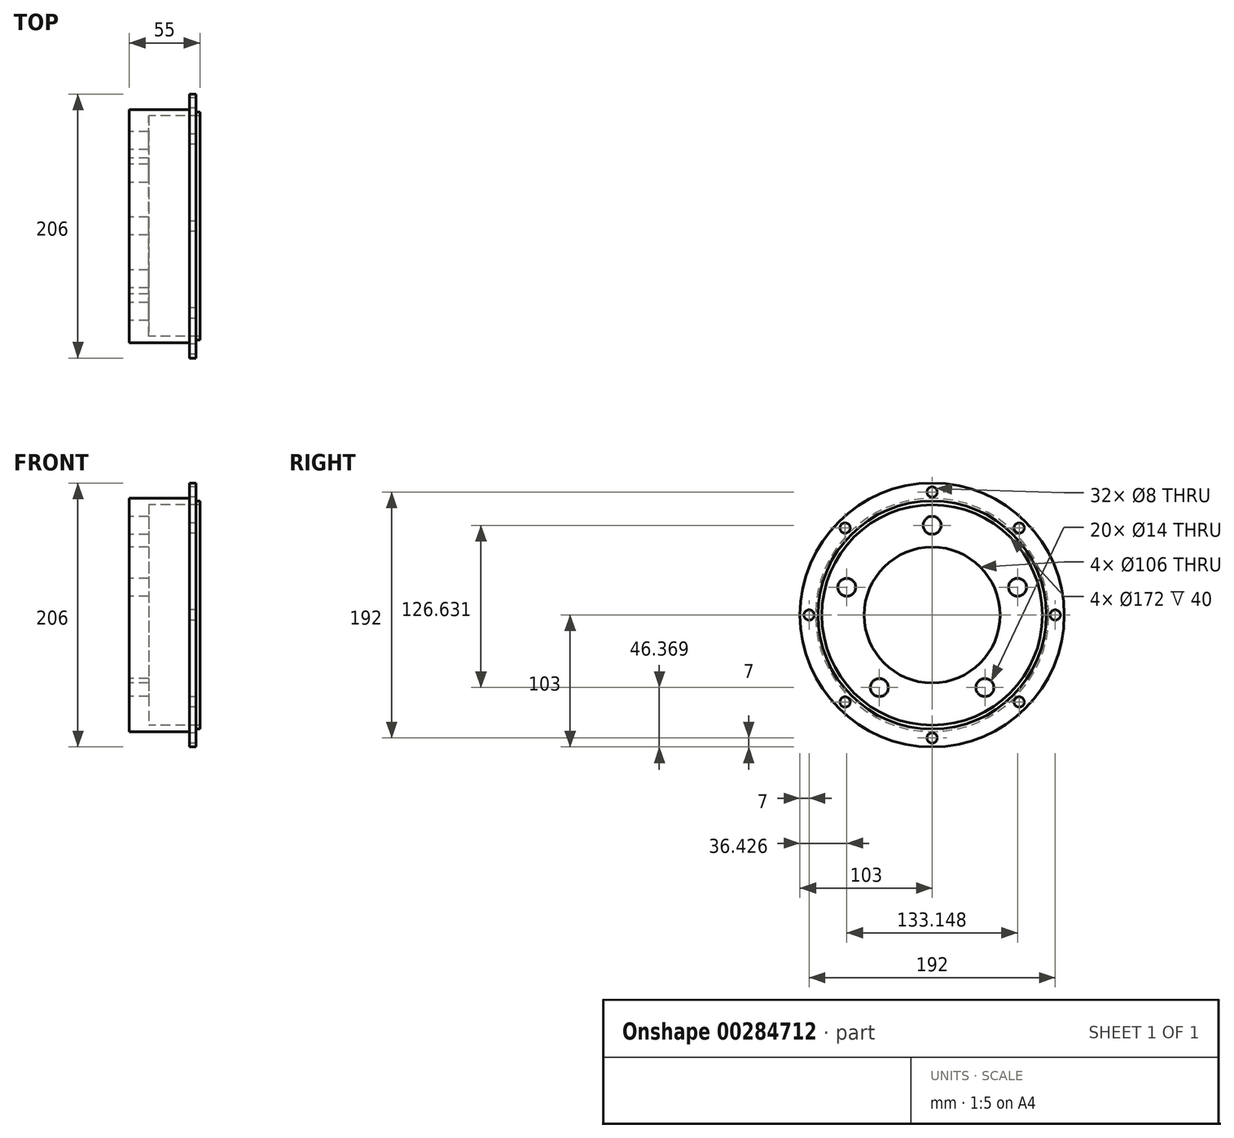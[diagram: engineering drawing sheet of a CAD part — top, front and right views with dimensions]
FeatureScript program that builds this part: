
annotation { "Feature Type Name" : "Feature", "Feature Type Description" : "" }
export const myFeature = defineFeature(function(context is Context, id is Id, definition is map)
    precondition{}
    {
        {
            var Q0;
            Q0=qCreatedBy(makeId("Front.planeOp"),FACE);
            var sketch = newSketch(context, id + "F0", { "sketchPlane" : qUnion([Q0])});
            skLineSegment(sketch, "E0", {"start": v(0, 53) * mm, "end": v(0, 91) * mm});
            skLineSegment(sketch, "E1", {"start": v(47, 103) * mm, "end": v(52, 103) * mm});
            skLineSegment(sketch, "E2", {"start": v(52, 103) * mm, "end": v(52, 89) * mm});
            skLineSegment(sketch, "E3", {"start": v(52, 86) * mm, "end": v(15, 86) * mm});
            skLineSegment(sketch, "E4", {"start": v(15, 86) * mm, "end": v(15, 53) * mm});
            skLineSegment(sketch, "E5", {"start": v(15, 53) * mm, "end": v(0, 53) * mm});
            skPoint(sketch, "E6", {"position": v(52, 93.5) * mm});
            skPoint(sketch, "E7", {"position": v(15, 70) * mm});
            skLineSegment(sketch, "E8", {"start": v(47, 103) * mm, "end": v(47, 91) * mm});
            skLineSegment(sketch, "E9", {"start": v(47, 91) * mm, "end": v(0, 91) * mm});
            skLineSegment(sketch, "E10", {"start": v(52, 86) * mm, "end": v(55, 86) * mm});
            skLineSegment(sketch, "E11", {"start": v(55, 86) * mm, "end": v(55, 89) * mm});
            skLineSegment(sketch, "E12", {"start": v(55, 89) * mm, "end": v(52, 89) * mm});
            skSolve(sketch);
        }
        {
            var Q0;
            Q0=qCreatedBy(makeId("Front.planeOp"),FACE);
            var sketch = newSketch(context, id + "F1", { "sketchPlane" : qUnion([Q0])});
            skLineSegment(sketch, "E13", {"start": v(-69.52, 0) * mm, "end": v(77.46, 0) * mm, "construction": true});
            skSolve(sketch);
        }
        {
            var Q0;
            Q0=qSketchRegion(id+"F0",true);
            var Q1;
            Q1=sQuery(id+"F1.wireOp",EDGE,"E13");
            revolve(context, id + "F2", {"entities" : qUnion([Q0]), "axis" : qUnion([Q1]), "revolveType" : RevolveType.FULL});
        }
        {
            var Q0;
            Q0=makeQuery(id+"F2.opRevolve","SWEPT_FACE",FACE,{"disambiguationData":[OSD([sQuery(id+"F0.wireOp",EDGE,"E0")])]});
            var sketch = newSketch(context, id + "F3", { "sketchPlane" : qUnion([Q0])});
            skCircle(sketch, "E14", {"center": v(0, 70) * mm, "radius": 7 * mm});
            skCircle(sketch, "E15.1.0", {"center": v(-66.57, 21.63) * mm, "radius": 7 * mm});
            skCircle(sketch, "E15.2.0", {"center": v(-41.14, -56.63) * mm, "radius": 7 * mm});
            skCircle(sketch, "E15.3.0", {"center": v(41.14, -56.63) * mm, "radius": 7 * mm});
            skCircle(sketch, "E15.4.0", {"center": v(66.57, 21.63) * mm, "radius": 7 * mm});
            skPoint(sketch, "E15.center", {"position": v(0, 0) * mm});
            skCircle(sketch, "E16", {"center": v(0, 0) * mm, "radius": 70 * mm, "construction": true});
            skSolve(sketch);
        }
        {
            var Q0;
            Q0=qSketchRegion(id+"F3",true);
            extrude(context, id + "F4", {"entities" : qUnion([Q0]), "operationType" : NewBodyOperationType.REMOVE, "oppositeDirection" : true, "depth" : 15 * mm});
        }
        {
            var Q0;
            Q0=makeQuery(id+"F2.opRevolve","SWEPT_FACE",FACE,{"disambiguationData":[OSD([sQuery(id+"F0.wireOp",EDGE,"E8")])]});
            var sketch = newSketch(context, id + "F5", { "sketchPlane" : qUnion([Q0])});
            skCircle(sketch, "E17", {"center": v(0, 96) * mm, "radius": 4 * mm});
            skLineSegment(sketch, "E18", {"start": v(0, 91) * mm, "end": v(0, 103) * mm, "construction": true});
            skCircle(sketch, "E19.1.0", {"center": v(-67.88, 67.88) * mm, "radius": 4 * mm});
            skCircle(sketch, "E19.2.0", {"center": v(-96, 0) * mm, "radius": 4 * mm});
            skCircle(sketch, "E19.3.0", {"center": v(-67.88, -67.88) * mm, "radius": 4 * mm});
            skCircle(sketch, "E19.4.0", {"center": v(0, -96) * mm, "radius": 4 * mm});
            skCircle(sketch, "E19.5.0", {"center": v(67.88, -67.88) * mm, "radius": 4 * mm});
            skCircle(sketch, "E19.6.0", {"center": v(96, 0) * mm, "radius": 4 * mm});
            skCircle(sketch, "E19.7.0", {"center": v(67.88, 67.88) * mm, "radius": 4 * mm});
            skPoint(sketch, "E19.center", {"position": v(0, 0) * mm});
            skCircle(sketch, "E20", {"center": v(0, 0) * mm, "radius": 96 * mm, "construction": true});
            skSolve(sketch);
        }
        {
            var Q0;
            Q0=qSketchRegion(id+"F5",true);
            extrude(context, id + "F6", {"entities" : qUnion([Q0]), "operationType" : NewBodyOperationType.REMOVE, "oppositeDirection" : true, "depth" : 5 * mm});
        }
    });
